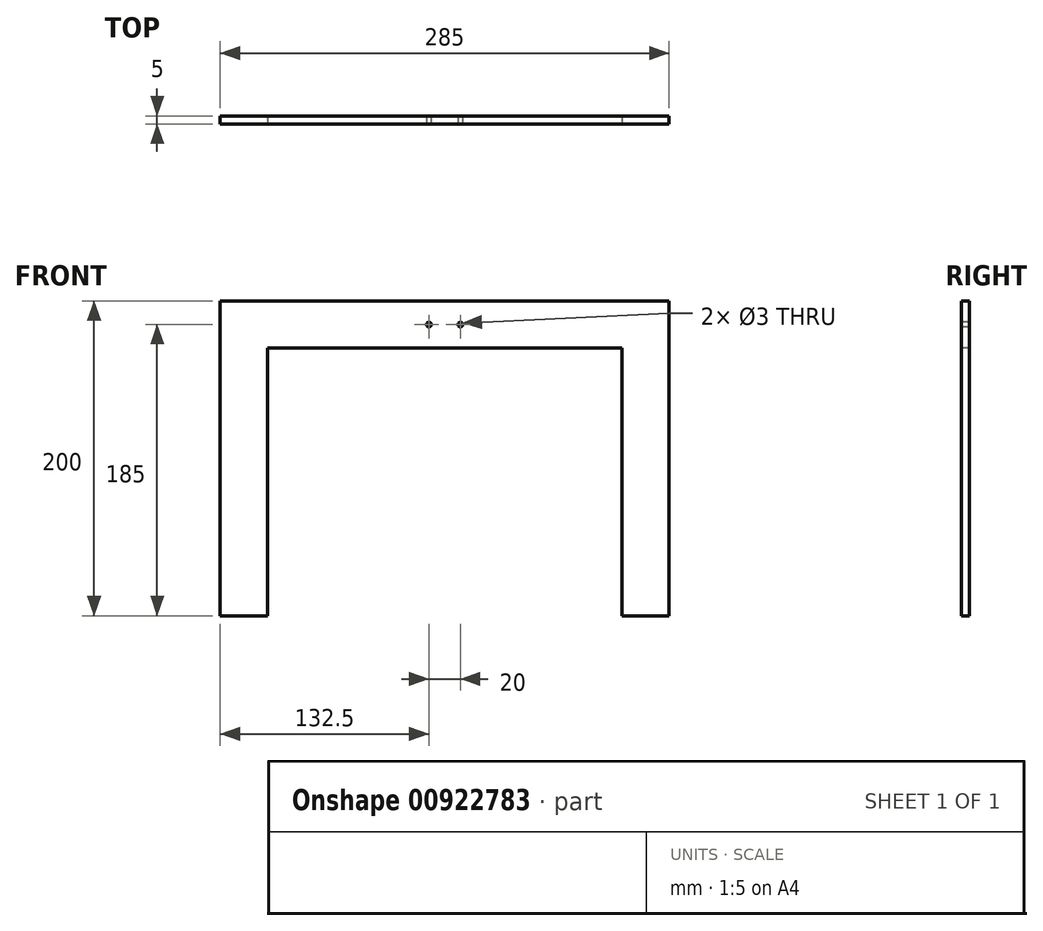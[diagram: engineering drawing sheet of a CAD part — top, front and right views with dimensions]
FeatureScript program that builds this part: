
annotation { "Feature Type Name" : "Feature", "Feature Type Description" : "" }
export const myFeature = defineFeature(function(context is Context, id is Id, definition is map)
    precondition{}
    {
        {
            var Q0;
            Q0=qCreatedBy(makeId("Front.planeOp"),FACE);
            var sketch = newSketch(context, id + "F0", { "sketchPlane" : qUnion([Q0])});
            skLineSegment(sketch, "E0.bottom", {"start": v(-142.5, 100) * mm, "end": v(142.5, 100) * mm});
            skLineSegment(sketch, "E0.top", {"start": v(-142.5, -100) * mm, "end": v(142.5, -100) * mm});
            skLineSegment(sketch, "E0.left", {"start": v(-142.5, 100) * mm, "end": v(-142.5, -100) * mm});
            skLineSegment(sketch, "E0.right", {"start": v(142.5, 100) * mm, "end": v(142.5, -100) * mm});
            skSolve(sketch);
        }
        {
            var Q0;
            Q0 = qSketchRegion(id + "F0", true);
            extrude(context, id + "F1", {"entities" : qUnion([Q0]), "depth" : 5 * mm, "offsetDistance" : 25 * mm});
        }
        {
            var Q0;
            Q0=makeQuery(id+"F1.opExtrude","CAP_FACE",FACE,{"disambiguationData":[OSD([sQuery(id+"F0.wireOp",EDGE,"E0.bottom"),sQuery(id+"F0.wireOp",EDGE,"E0.top"),sQuery(id+"F0.wireOp",EDGE,"E0.left"),sQuery(id+"F0.wireOp",EDGE,"E0.right")])],"isStart":false});
            var sketch = newSketch(context, id + "F2", { "sketchPlane" : qUnion([Q0])});
            skLineSegment(sketch, "E1", {"start": v(-112.5, -100) * mm, "end": v(-112.5, 70) * mm});
            skLineSegment(sketch, "E2", {"start": v(-112.5, 70) * mm, "end": v(112.5, 70) * mm});
            skLineSegment(sketch, "E3", {"start": v(112.5, 70) * mm, "end": v(112.5, -100) * mm});
            skLineSegment(sketch, "E4", {"start": v(-112.5, -100) * mm, "end": v(112.5, -100) * mm});
            skSolve(sketch);
        }
        {
            var Q0;
            Q0=makeQuery(id+"F2.imprint","IMPRINT",FACE,{"disambiguationData":[TD([[makeQuery(id+"F2.imprint","IMPRINT",EDGE,{"derivedFrom":sQuery(id+"F2.wireOp",EDGE,"E1")}),-1.0]])]});
            extrude(context, id + "F3", {"entities" : qUnion([Q0]), "operationType" : NewBodyOperationType.REMOVE, "oppositeDirection" : true, "depth" : 25 * mm, "offsetDistance" : 25 * mm});
        }
        {
            var Q0;
            Q0=makeQuery(id+"F1.opExtrude","CAP_FACE",FACE,{"disambiguationData":[OSD([sQuery(id+"F0.wireOp",EDGE,"E0.bottom"),sQuery(id+"F0.wireOp",EDGE,"E0.top"),sQuery(id+"F0.wireOp",EDGE,"E0.left"),sQuery(id+"F0.wireOp",EDGE,"E0.right")])],"isStart":false});
            var sketch = newSketch(context, id + "F4", { "sketchPlane" : qUnion([Q0])});
            skCircle(sketch, "E5", {"center": v(-10, 85) * mm, "radius": 1.5 * mm});
            skCircle(sketch, "E6", {"center": v(10, 85) * mm, "radius": 1.5 * mm});
            skSolve(sketch);
        }
        {
            var Q0;
            Q0=makeQuery(id+"F4.imprint","IMPRINT",FACE,{"disambiguationData":[TD([[makeQuery(id+"F4.imprint","IMPRINT",EDGE,{"derivedFrom":sQuery(id+"F4.wireOp",EDGE,"E5")}),1.0]])]});
            var Q1;
            Q1=makeQuery(id+"F4.imprint","IMPRINT",FACE,{"disambiguationData":[TD([[makeQuery(id+"F4.imprint","IMPRINT",EDGE,{"derivedFrom":sQuery(id+"F4.wireOp",EDGE,"E6")}),1.0]])]});
            extrude(context, id + "F5", {"entities" : qUnion([Q0, Q1]), "operationType" : NewBodyOperationType.REMOVE, "oppositeDirection" : true, "depth" : 25 * mm, "offsetDistance" : 25 * mm});
        }
    });
